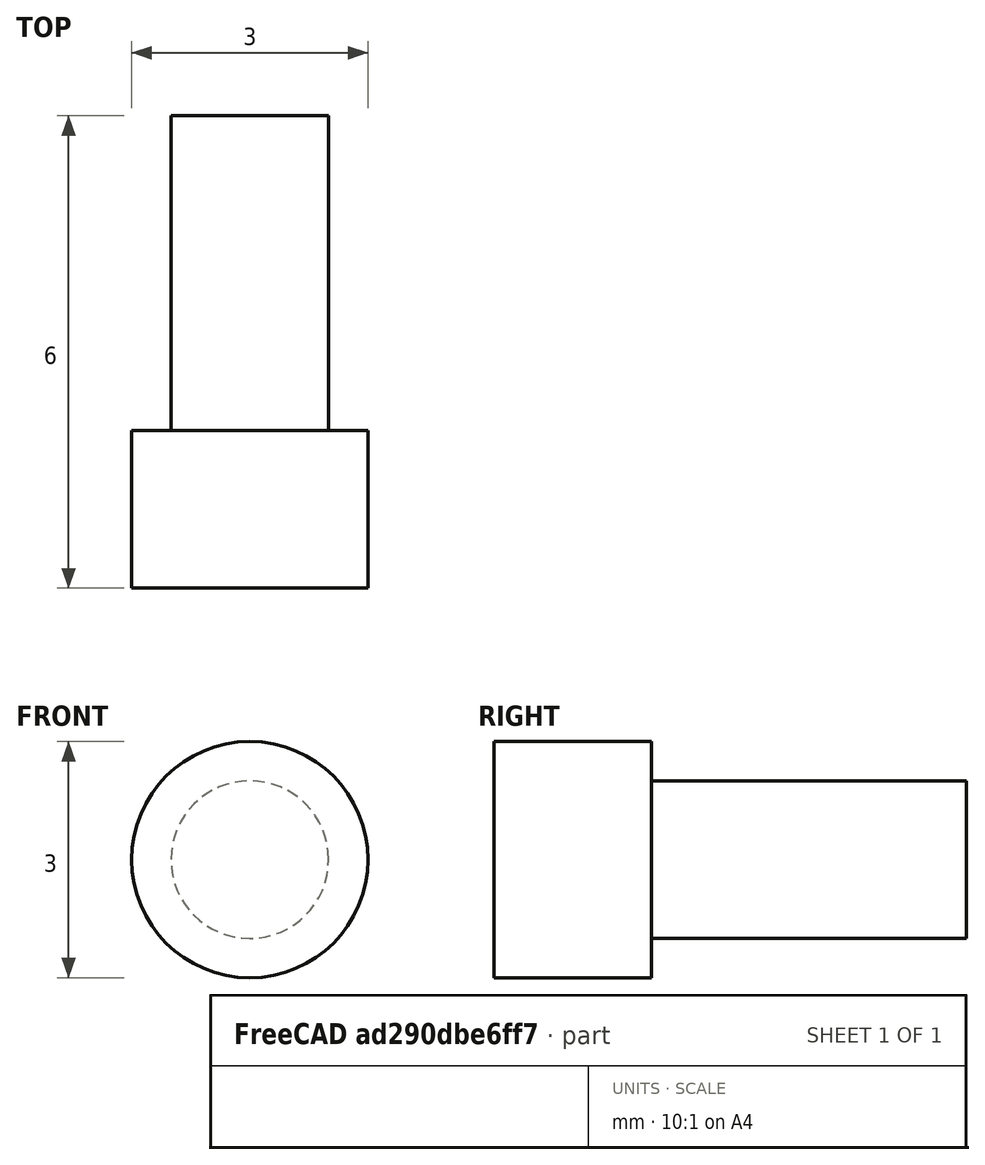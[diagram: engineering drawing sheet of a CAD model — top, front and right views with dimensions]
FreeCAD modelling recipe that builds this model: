
FCSTD DOCUMENT  (FreeCAD 1.0R39319 (Git))
Label: visM2L4
License: All rights reserved
LicenseURL: https://en.wikipedia.org/wiki/All_rights_reserved
objects: Sketcher::SketchObject×1, PartDesign::Revolution×1, PartDesign::Body×1
note: 6 computed .brp shape members not serialized (recipe doc carries the construction recipe); baked Part::Feature solids carry a one-line shape summary decoded from their .brp

FEATURE [Sketcher::SketchObject] Sketch
  ArcFitTolerance = 1e-06
  AttachmentSupport = -> [YZ_Plane]
  FullyConstrained = true
  MakeInternals = false
  MapMode = 5
  Placement = pos=(0,0,0) rot=(0.57735,0.57735,0.57735;2.0944rad)
  sketch-geometry (6):
    g0: LineSegment StartX=-2 StartY=0 StartZ=0 EndX=-2 EndY=1.5 EndZ=0
    g1: LineSegment StartX=-2 StartY=1.5 StartZ=0 EndX=-4.574e-13 EndY=1.5 EndZ=0
    g2: LineSegment StartX=-4.574e-13 StartY=1.5 StartZ=0 EndX=0 EndY=1 EndZ=0
    g3: LineSegment StartX=0 StartY=1 StartZ=0 EndX=4 EndY=1 EndZ=0
    g4: LineSegment StartX=4 StartY=0 StartZ=0 EndX=4 EndY=1 EndZ=0
    g5: LineSegment StartX=-2 StartY=0 StartZ=0 EndX=4 EndY=0 EndZ=0
  constraints (18):
    c: PointOnObject(g0,g-1)
    c: Vertical(g0)
    c: Coincident(g1,g0)
    c: PointOnObject(g1,g-2)
    c: Horizontal(g1)
    c: Coincident(g2,g1)
    c: PointOnObject(g2,g-2)
    c: Coincident(g3,g2)
    c: Horizontal(g3)
    c: PointOnObject(g4,g-1)
    c: Coincident(g5,g0)
    c: Coincident(g5,g4)
    c: Coincident(g4,g3)
    c: Perpendicular(g-1,g4)
    c: DistanceY(g0,g0) = 1.5
    c: DistanceX(g1,g1) = 2
    c: DistanceX(g3,g3) = 4
    c: DistanceY(g4,g4) = 1
FEATURE [PartDesign::Revolution] Revolution
  Angle = 360
  Angle2 = 60
  Axis = (1e-16,1,-1e-16)
  Base = (0,0,0)
  Placement = pos=(0,0,0) rot=(1,1,1;2.0944rad)
  Profile = -> Sketch
  ReferenceAxis = -> Y_Axis
  Refine = true
  Suppressed = false
  Type = 0
FEATURE [PartDesign::Body] Body  label="Corps"
  AllowCompound = false
  Group = -> [Sketch,Revolution]
  Origin = -> Origin
  Tip = -> Revolution
